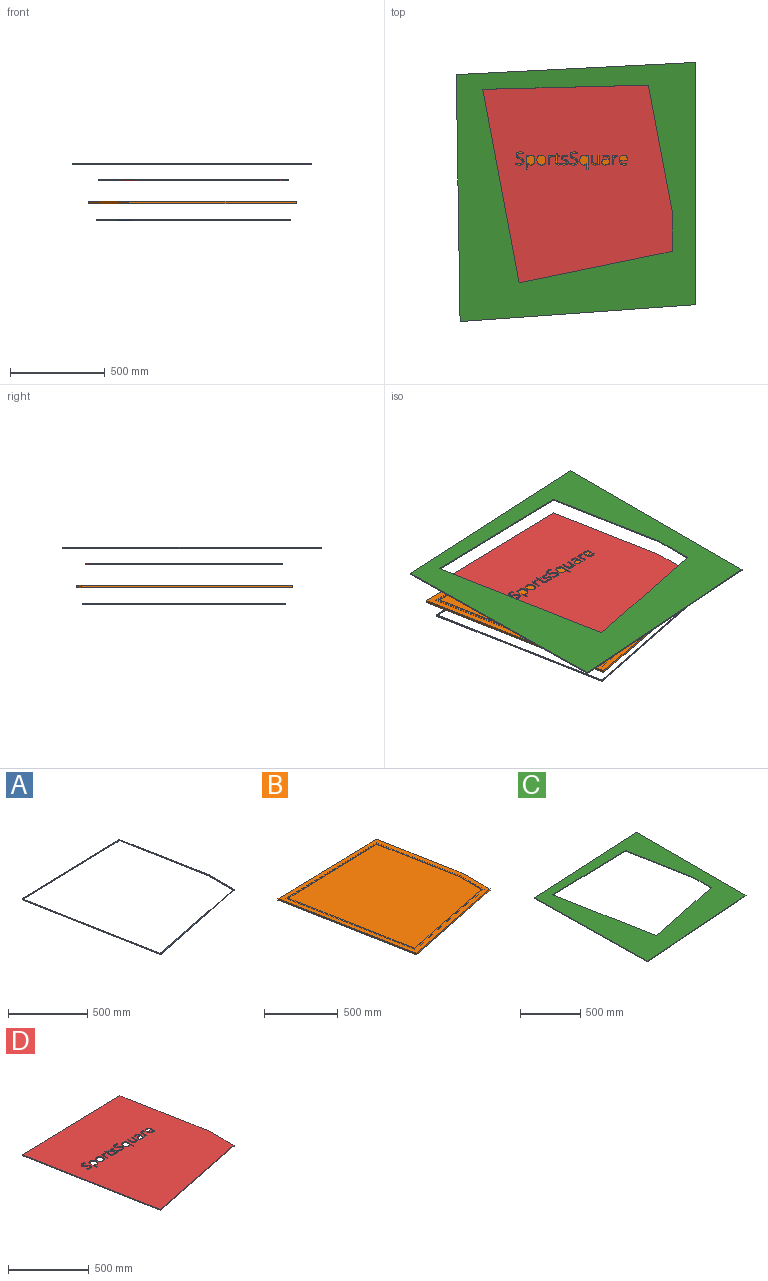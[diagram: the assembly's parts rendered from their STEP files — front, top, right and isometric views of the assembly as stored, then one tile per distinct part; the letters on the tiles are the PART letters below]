
ASSEMBLY  parts=4 mates=3
PART A: 22 faces, bbox 1023.6x1068.1x5 mm
  f0: cylinder r=5mm len=5.04mm, axis (0,0,-1), area 35.3mm2, adj f1,f19,f20,f21
  f1: plane 667.31x125.75mm, normal (-0.98,-0.19,0), area 3395.3mm2, adj f0,f2,f20,f21
  f2: cylinder r=5mm len=5mm, axis (0,0,-1), area 4.7mm2, adj f1,f3,f20,f21
  f3: plane 215x5mm, normal (-1,0,0), area 1075mm2, adj f2,f4,f20,f21
  f4: cylinder r=5mm len=5mm, axis (0,0,-1), area 34.2mm2, adj f3,f5,f20,f21
  f5: plane 812.02x166.92mm, normal (-0.2,0.98,0), area 4145mm2, adj f4,f6,f20,f21
  f6: cylinder r=5mm len=5.92mm, axis (0,0,-1), area 39.7mm2, adj f5,f7,f20,f21
  f7: plane 1026.83x192.78mm, normal (0.98,0.18,0), area 5223.8mm2, adj f6,f8,f20,f21
  f8: cylinder r=5mm len=5.92mm, axis (0,0,-1), area 43.3mm2, adj f7,f19,f20,f21
  f9: plane 671.02x126.45mm, normal (0.98,0.19,0), area 3414.1mm2, adj f10,f18,f20,f21
  f10: cylinder r=5mm len=5.04mm, axis (0,0,-1), area 35.3mm2, adj f9,f11,f20,f21
  f11: plane 887.15x22.61mm, normal (-0.03,1,0), area 4437.2mm2, adj f10,f12,f20,f21
  f12: cylinder r=5mm len=5.92mm, axis (0,0,-1), area 43.3mm2, adj f11,f13,f20,f21
  f13: plane 1035.44x194.39mm, normal (-0.98,-0.18,0), area 5267.7mm2, adj f12,f14,f20,f21
  f14: cylinder r=5mm len=5.92mm, axis (0,0,-1), area 39.7mm2, adj f13,f15,f20,f21
  f15: plane 819.2x168.4mm, normal (0.2,-0.98,0), area 4181.7mm2, adj f14,f16,f20,f21
  f16: cylinder r=5mm len=5mm, axis (0,0,-1), area 34.2mm2, adj f15,f17,f20,f21
  f17: plane 218.64x5mm, normal (1,0,0), area 1093.2mm2, adj f16,f18,f20,f21
  f18: cylinder r=5mm len=5mm, axis (0,0,-1), area 4.7mm2, adj f9,f17,f20,f21
  f19: plane 879.05x22.4mm, normal (0.03,-1,0), area 4396.7mm2, adj f0,f8,f20,f21
  f20: plane 1068.05x1023.6mm, normal (0,0,1), area 14809.9mm2, adj f0,f1,f2,f3,f4,f5,f6,f7
  f21: plane 1068.05x1023.6mm, normal (0,0,-1), area 14809.9mm2, adj f0,f1,f2,f3,f4,f5,f6,f7
PART B: 25 faces, bbox 1096.8x1141.5x12 mm
  f0: plane 964.09x24.57mm, normal (-0.03,1,0), area 11572.8mm2, adj f1,f9,f10,f11
  f1: plane 1116.92x209.69mm, normal (-0.98,-0.18,0), area 13637.2mm2, adj f0,f2,f10,f11
  f2: plane 887.09x182.36mm, normal (0.2,-0.98,0), area 10867.6mm2, adj f1,f3,f10,f11
  f3: plane 254.98x12mm, normal (1,0,0), area 3059.8mm2, adj f2,f9,f10,f11
  f4: plane 1022.14x191.9mm, normal (0.98,0.18,0), area 2080mm2, adj f5,f8,f10,f12
  f5: plane 875x22.3mm, normal (0.03,-1,0), area 1750.6mm2, adj f4,f6,f10,f12
  f6: plane 663.33x125mm, normal (-0.98,-0.19,0), area 1350mm2, adj f5,f7,f10,f12
  f7: plane 215x2mm, normal (-1,0,0), area 430mm2, adj f6,f8,f10,f12
  f8: plane 808.1x166.12mm, normal (-0.2,0.98,0), area 1650mm2, adj f4,f7,f10,f12
  f9: plane 704.16x132.69mm, normal (0.98,0.19,0), area 8598.6mm2, adj f0,f3,f10,f11
  f10: plane 1141.5x1096.78mm, normal (0,0,1), area 167382.4mm2, adj f0,f1,f2,f3,f4,f5,f6,f7
  f11: plane 1141.5x1096.78mm, normal (0,0,-1), area 119520.9mm2, adj f0,f1,f2,f3,f9,f17,f18,f19
  f12: plane 1044.44x1000mm, normal (0,0,1), area 828035.3mm2, adj f4,f5,f6,f7,f8
  f13: plane 885.12x22.56mm, normal (-0.03,1,0), area 7968.7mm2, adj f14,f22,f23,f24
  f14: plane 667.96x125.87mm, normal (0.98,0.19,0), area 6117.5mm2, adj f13,f15,f23,f24
  f15: plane 219.54x9mm, normal (1,0,0), area 1975.9mm2, adj f14,f16,f23,f24
  f16: plane 817.08x167.96mm, normal (0.2,-0.98,0), area 7507.5mm2, adj f15,f22,f23,f24
  f17: plane 675.39x127.27mm, normal (-0.98,-0.19,0), area 6185.5mm2, adj f11,f18,f21,f23
  f18: plane 901.32x22.97mm, normal (0.03,-1,0), area 8114.5mm2, adj f11,f17,f19,f23
  f19: plane 1050.15x197.16mm, normal (0.98,0.18,0), area 9616.4mm2, adj f11,f18,f20,f23
  f20: plane 831.44x170.92mm, normal (-0.2,0.98,0), area 7639.4mm2, adj f11,f19,f21,f23
  f21: plane 226.81x9mm, normal (-1,0,0), area 2041.3mm2, adj f11,f17,f20,f23
  f22: plane 1032.91x193.92mm, normal (-0.98,-0.18,0), area 9458.6mm2, adj f13,f16,f23,f24
  f23: plane 1073.12x1028.59mm, normal (0,0,-1), area 29611.3mm2, adj f13,f14,f15,f16,f17,f18,f19,f20
  f24: plane 1055.47x1011mm, normal (0,0,-1), area 846285.5mm2, adj f13,f14,f15,f16,f22
PART C: 11 faces, bbox 1265x1369.2x6 mm
  f0: plane 1022.14x191.9mm, normal (0.98,0.18,0), area 6240mm2, adj f1,f8,f9,f10
  f1: plane 875x22.3mm, normal (0.03,-1,0), area 5251.7mm2, adj f0,f2,f9,f10
  f2: plane 663.33x125mm, normal (-0.98,-0.19,0), area 4050mm2, adj f1,f3,f9,f10
  f3: plane 215x6mm, normal (-1,0,0), area 1290mm2, adj f2,f8,f9,f10
  f4: plane 1265x64.18mm, normal (-0.05,1,0), area 7599.8mm2, adj f5,f7,f9,f10
  f5: plane 1305x20mm, normal (-1,-0.02,0), area 7830.9mm2, adj f4,f6,f9,f10
  f6: plane 1245x89.18mm, normal (0.07,-1,0), area 7489.1mm2, adj f5,f7,f9,f10
  f7: plane 1280x6mm, normal (1,0,0), area 7680mm2, adj f4,f6,f9,f10
  f8: plane 808.1x166.12mm, normal (-0.2,0.98,0), area 4950mm2, adj f0,f3,f9,f10
  f9: plane 1369.18x1265mm, normal (0,0,1), area 794819mm2, adj f0,f1,f2,f3,f4,f5,f6,f7
  f10: plane 1369.18x1265mm, normal (0,0,-1), area 794819mm2, adj f0,f1,f2,f3,f4,f5,f6,f7
PART D: 216 faces, bbox 1000x1044.4x6 mm
  f0: extruded ~11.31x6mm, area 73.7mm2, adj f1,f213,f214,f215
  f1: extruded ~13.96x6.49mm, area 96mm2, adj f0,f2,f214,f215
  f2: extruded ~17.62x6mm, area 112mm2, adj f1,f3,f214,f215
  f3: extruded ~18.55x6mm, area 113.7mm2, adj f2,f4,f214,f215
  f4: plane 7.6x6mm, normal (1,0,0), area 45.6mm2, adj f3,f5,f214,f215
  f5: extruded ~9.1x6mm, area 57.2mm2, adj f4,f6,f214,f215
  f6: extruded ~9.74x6mm, area 58.8mm2, adj f5,f7,f214,f215
  f7: extruded ~11.87x6mm, area 74.7mm2, adj f6,f8,f214,f215
  f8: extruded ~8.33x6mm, area 57.7mm2, adj f7,f9,f214,f215
  f9: extruded ~6x5.77mm, area 36.1mm2, adj f8,f10,f214,f215
  f10: extruded ~6x4.73mm, area 38.2mm2, adj f9,f11,f214,f215
  f11: extruded ~10.08x6mm, area 65.9mm2, adj f10,f12,f214,f215
  f12: extruded ~13.51x8.02mm, area 95.2mm2, adj f11,f13,f214,f215
  f13: extruded ~12.1x6mm, area 78.3mm2, adj f12,f14,f214,f215
  f14: extruded ~12.47x6mm, area 85.9mm2, adj f13,f15,f214,f215
  f15: extruded ~15.59x6mm, area 99.5mm2, adj f14,f16,f214,f215
  f16: extruded ~18.59x6mm, area 114.6mm2, adj f15,f17,f214,f215
  f17: plane 6.86x6mm, normal (-0.94,0.34,0), area 43.7mm2, adj f16,f18,f214,f215
  f18: extruded ~16.32x6mm, area 100.9mm2, adj f17,f19,f214,f215
  f19: extruded ~9.79x6mm, area 62mm2, adj f18,f20,f214,f215
  f20: extruded ~7.46x6mm, area 51.5mm2, adj f19,f21,f214,f215
  f21: extruded ~6x5.77mm, area 35.9mm2, adj f20,f22,f214,f215
  f22: extruded ~6x4.39mm, area 36.5mm2, adj f21,f23,f214,f215
  f23: extruded ~9.44x6mm, area 61.9mm2, adj f22,f213,f214,f215
  f24: extruded ~15.52x6.94mm, area 105.7mm2, adj f25,f201,f214,f215
  f25: extruded ~9.07x6mm, area 56mm2, adj f24,f26,f214,f215
  f26: extruded ~6.88x6mm, area 54mm2, adj f25,f27,f214,f215
  f27: plane 6x0.56mm, normal (0,1,0), area 3.4mm2, adj f26,f28,f214,f215
  f28: extruded ~8.44x6mm, area 50.8mm2, adj f27,f29,f214,f215
  f29: plane 20.92x6mm, normal (-1,0,0), area 125.5mm2, adj f28,f30,f214,f215
  f30: plane 7.7x6mm, normal (0,1,0), area 46.2mm2, adj f29,f31,f214,f215
  f31: plane 73.65x6mm, normal (1,0,0), area 441.9mm2, adj f30,f32,f214,f215
  f32: plane 6.26x6mm, normal (0,-1,0), area 37.6mm2, adj f31,f33,f214,f215
  f33: plane 6.96x6mm, normal (-0.99,-0.15,0), area 42.2mm2, adj f32,f34,f214,f215
  f34: plane 6x0.37mm, normal (0,-1,0), area 2.2mm2, adj f33,f35,f214,f215
  f35: extruded ~6.91x6.04mm, area 55.7mm2, adj f34,f36,f214,f215
  f36: extruded ~9.05x6mm, area 55.9mm2, adj f35,f37,f214,f215
  f37: extruded ~15.6x6.92mm, area 106.2mm2, adj f36,f38,f214,f215
  f38: extruded ~19.38x6mm, area 123.2mm2, adj f37,f201,f214,f215
  f39: extruded ~8.77x6mm, area 55.9mm2, adj f40,f202,f214,f215
  f40: extruded ~6.07x6mm, area 36.6mm2, adj f39,f41,f214,f215
  f41: plane 7.14x6mm, normal (-0.99,0.15,0), area 43.3mm2, adj f40,f42,f214,f215
  f42: extruded ~6x5.57mm, area 33.7mm2, adj f41,f43,f214,f215
  f43: extruded ~10.55x6mm, area 72.4mm2, adj f42,f44,f214,f215
  f44: extruded ~12.47x6mm, area 81.1mm2, adj f43,f45,f214,f215
  f45: plane 27.28x6mm, normal (-1,0,0), area 163.7mm2, adj f44,f46,f214,f215
  f46: plane 7.7x6mm, normal (0,1,0), area 46.2mm2, adj f45,f47,f214,f215
  f47: plane 50.83x6mm, normal (1,0,0), area 305mm2, adj f46,f48,f214,f215
  f48: plane 6.35x6mm, normal (0,-1,0), area 38.1mm2, adj f47,f49,f214,f215
  f49: plane 9.41x6mm, normal (-1,-0.09,0), area 56.7mm2, adj f48,f50,f214,f215
  f50: plane 6x0.37mm, normal (0,-1,0), area 2.2mm2, adj f49,f202,f214,f215
  f51: extruded ~6x5.98mm, area 40mm2, adj f52,f203,f214,f215
  f52: extruded ~6x3.95mm, area 23.8mm2, adj f51,f53,f214,f215
  f53: extruded ~6x3.01mm, area 18.5mm2, adj f52,f54,f214,f215
  f54: plane 6x5.89mm, normal (-1,0,0), area 35.3mm2, adj f53,f55,f214,f215
  f55: extruded ~6x3.68mm, area 22.9mm2, adj f54,f56,f214,f215
  f56: extruded ~6x4.39mm, area 26.5mm2, adj f55,f57,f214,f215
  f57: extruded ~15.54x14.74mm, area 147.4mm2, adj f56,f58,f214,f215
  f58: plane 30.24x6mm, normal (1,0,0), area 181.5mm2, adj f57,f59,f214,f215
  f59: plane 7.29x6mm, normal (0,1,0), area 43.7mm2, adj f58,f60,f214,f215
  f60: plane 6x3.71mm, normal (1,0,0), area 22.3mm2, adj f59,f61,f214,f215
  f61: plane 7.29x6mm, normal (0.4,-0.92,0), area 47.8mm2, adj f60,f62,f214,f215
  f62: plane 10.85x6mm, normal (0.96,-0.29,0), area 67.9mm2, adj f61,f63,f214,f215
  f63: plane 6x4.45mm, normal (0,-1,0), area 26.7mm2, adj f62,f64,f214,f215
  f64: plane 11.78x6mm, normal (-1,0,0), area 70.7mm2, adj f63,f65,f214,f215
  f65: plane 14.75x6mm, normal (0,-1,0), area 88.5mm2, adj f64,f66,f214,f215
  f66: plane 6x5.98mm, normal (-1,0,0), area 35.9mm2, adj f65,f67,f214,f215
  f67: plane 14.75x6mm, normal (0,1,0), area 88.5mm2, adj f66,f68,f214,f215
  f68: plane 29.92x6mm, normal (-1,0,0), area 179.5mm2, adj f67,f203,f214,f215
  f69: extruded ~8.4x6mm, area 55.3mm2, adj f70,f204,f214,f215
  f70: extruded ~10.94x6mm, area 75.9mm2, adj f69,f71,f214,f215
  f71: extruded ~14.84x6mm, area 93.5mm2, adj f70,f72,f214,f215
  f72: extruded ~15.76x6mm, area 97.5mm2, adj f71,f73,f214,f215
  f73: plane 7.14x6mm, normal (1,0,0), area 42.8mm2, adj f72,f74,f214,f215
  f74: extruded ~7.86x6mm, area 50.4mm2, adj f73,f75,f214,f215
  f75: extruded ~8.1x6mm, area 49.1mm2, adj f74,f76,f214,f215
  f76: extruded ~9.27x6mm, area 57.4mm2, adj f75,f77,f214,f215
  f77: extruded ~6x5.87mm, area 42.3mm2, adj f76,f78,f214,f215
  f78: extruded ~6x5.08mm, area 35.4mm2, adj f77,f79,f214,f215
  f79: extruded ~10.05x6mm, area 67.5mm2, adj f78,f80,f214,f215
  f80: extruded ~10.08x6mm, area 66.7mm2, adj f79,f81,f214,f215
  f81: extruded ~6x4.47mm, area 38.2mm2, adj f80,f82,f214,f215
  f82: extruded ~6x5.97mm, area 37.3mm2, adj f81,f83,f214,f215
  f83: extruded ~9.82x6mm, area 69.1mm2, adj f82,f84,f214,f215
  f84: extruded ~13.86x6mm, area 87.3mm2, adj f83,f85,f214,f215
  f85: extruded ~16.06x6mm, area 99.1mm2, adj f84,f86,f214,f215
  f86: plane 6.26x6mm, normal (-0.92,0.4,0), area 41mm2, adj f85,f87,f214,f215
  f87: extruded ~13.86x6mm, area 85.8mm2, adj f86,f88,f214,f215
  f88: extruded ~8.26x6mm, area 51.2mm2, adj f87,f89,f214,f215
  f89: extruded ~6x4.73mm, area 34.5mm2, adj f88,f90,f214,f215
  f90: extruded ~6x3.48mm, area 22.2mm2, adj f89,f91,f214,f215
  f91: extruded ~6x3.36mm, area 26.2mm2, adj f90,f92,f214,f215
  f92: extruded ~8.9x6mm, area 58mm2, adj f91,f204,f214,f215
  f93: extruded ~11.31x6mm, area 73.7mm2, adj f94,f205,f214,f215
  f94: extruded ~13.96x6.49mm, area 96mm2, adj f93,f95,f214,f215
  f95: extruded ~17.62x6mm, area 112mm2, adj f94,f96,f214,f215
  f96: extruded ~18.55x6mm, area 113.7mm2, adj f95,f97,f214,f215
  f97: plane 7.6x6mm, normal (1,0,0), area 45.6mm2, adj f96,f98,f214,f215
  f98: extruded ~9.1x6mm, area 57.2mm2, adj f97,f99,f214,f215
  f99: extruded ~9.74x6mm, area 58.8mm2, adj f98,f100,f214,f215
  f100: extruded ~11.87x6mm, area 74.7mm2, adj f99,f101,f214,f215
  f101: extruded ~8.33x6mm, area 57.7mm2, adj f100,f102,f214,f215
  f102: extruded ~6x5.77mm, area 36.1mm2, adj f101,f103,f214,f215
  f103: extruded ~6x4.73mm, area 38.2mm2, adj f102,f104,f214,f215
  f104: extruded ~10.08x6mm, area 65.9mm2, adj f103,f105,f214,f215
  f105: extruded ~13.51x8.02mm, area 95.2mm2, adj f104,f106,f214,f215
  f106: extruded ~12.1x6mm, area 78.3mm2, adj f105,f107,f214,f215
  f107: extruded ~12.47x6mm, area 85.9mm2, adj f106,f108,f214,f215
  f108: extruded ~15.59x6mm, area 99.5mm2, adj f107,f109,f214,f215
  f109: extruded ~18.59x6mm, area 114.6mm2, adj f108,f110,f214,f215
  f110: plane 6.86x6mm, normal (-0.94,0.34,0), area 43.7mm2, adj f109,f111,f214,f215
  f111: extruded ~16.32x6mm, area 100.9mm2, adj f110,f112,f214,f215
  f112: extruded ~9.79x6mm, area 62mm2, adj f111,f113,f214,f215
  f113: extruded ~7.46x6mm, area 51.5mm2, adj f112,f114,f214,f215
  f114: extruded ~6x5.77mm, area 35.9mm2, adj f113,f115,f214,f215
  f115: extruded ~6x4.39mm, area 36.5mm2, adj f114,f116,f214,f215
  f116: extruded ~9.44x6mm, area 61.9mm2, adj f115,f205,f214,f215
  f117: extruded ~16.04x7.75mm, area 111.6mm2, adj f118,f206,f214,f215
  f118: extruded ~15.36x6.92mm, area 104.8mm2, adj f117,f119,f214,f215
  f119: extruded ~19.29x6mm, area 122.7mm2, adj f118,f120,f214,f215
  f120: extruded ~19.48x6mm, area 123.9mm2, adj f119,f121,f214,f215
  f121: extruded ~15.49x7mm, area 105.8mm2, adj f120,f122,f214,f215
  f122: extruded ~16.04x7.89mm, area 111.9mm2, adj f121,f123,f214,f215
  f123: plane 6x0.43mm, normal (0,-1,0), area 2.6mm2, adj f122,f124,f214,f215
  f124: plane 6.96x6mm, normal (0.99,-0.16,0), area 42.3mm2, adj f123,f125,f214,f215
  f125: plane 6.07x6mm, normal (0,-1,0), area 36.4mm2, adj f124,f126,f214,f215
  f126: plane 73.65x6mm, normal (-1,0,0), area 441.9mm2, adj f125,f127,f214,f215
  f127: plane 7.7x6mm, normal (0,1,0), area 46.2mm2, adj f126,f128,f214,f215
  f128: plane 21.76x6mm, normal (1,0,0), area 130.5mm2, adj f127,f129,f214,f215
  f129: extruded ~7.88x6mm, area 47.4mm2, adj f128,f206,f214,f215
  f130: plane 7.79x6mm, normal (0,-1,0), area 46.7mm2, adj f131,f207,f214,f215
  f131: plane 32.97x6mm, normal (-1,0,0), area 197.8mm2, adj f130,f132,f214,f215
  f132: extruded ~9.28x6mm, area 59.5mm2, adj f131,f133,f214,f215
  f133: extruded ~8.85x6mm, area 57.8mm2, adj f132,f134,f214,f215
  f134: extruded ~11.66x6mm, area 77.2mm2, adj f133,f135,f214,f215
  f135: extruded ~14.24x6mm, area 90mm2, adj f134,f136,f214,f215
  f136: plane 26.71x6mm, normal (1,0,0), area 160.3mm2, adj f135,f137,f214,f215
  f137: plane 7.7x6mm, normal (0,-1,0), area 46.2mm2, adj f136,f138,f214,f215
  f138: plane 50.83x6mm, normal (-1,0,0), area 305mm2, adj f137,f139,f214,f215
  f139: plane 6.35x6mm, normal (0,1,0), area 38.1mm2, adj f138,f140,f214,f215
  f140: plane 6.81x6mm, normal (0.99,0.16,0), area 41.4mm2, adj f139,f141,f214,f215
  f141: plane 6x0.42mm, normal (0,1,0), area 2.5mm2, adj f140,f142,f214,f215
  f142: extruded ~6.56x6mm, area 53.1mm2, adj f141,f143,f214,f215
  f143: extruded ~9.59x6mm, area 59.2mm2, adj f142,f144,f214,f215
  f144: extruded ~13.88x6mm, area 89.6mm2, adj f143,f145,f214,f215
  f145: extruded ~14.1x6mm, area 91.5mm2, adj f144,f207,f214,f215
  f146: plane 6x5.71mm, normal (0,1,0), area 34.3mm2, adj f147,f208,f214,f215
  f147: plane 7.24x6mm, normal (0.98,0.21,0), area 44.4mm2, adj f146,f148,f214,f215
  f148: plane 6x0.37mm, normal (0,1,0), area 2.2mm2, adj f147,f149,f214,f215
  f149: extruded ~7.58x6.48mm, area 60.4mm2, adj f148,f150,f214,f215
  f150: extruded ~9.45x6mm, area 58mm2, adj f149,f151,f214,f215
  f151: extruded ~11.84x6mm, area 76.6mm2, adj f150,f152,f214,f215
  f152: extruded ~11.09x6mm, area 73.5mm2, adj f151,f153,f214,f215
  f153: extruded ~24.62x16.13mm, area 198.4mm2, adj f152,f154,f214,f215
  f154: plane 8.62x6mm, normal (0.03,-1,0), area 51.8mm2, adj f153,f155,f214,f215
  f155: plane 6x3.16mm, normal (1,0,0), area 19mm2, adj f154,f156,f214,f215
  f156: extruded ~8.83x6mm, area 56.4mm2, adj f155,f157,f214,f215
  f157: extruded ~8.24x6mm, area 53.9mm2, adj f156,f158,f214,f215
  f158: extruded ~14.37x6mm, area 90mm2, adj f157,f159,f214,f215
  f159: plane 6x5.89mm, normal (0.93,0.37,0), area 38.1mm2, adj f158,f160,f214,f215
  f160: extruded ~8.23x6mm, area 53.1mm2, adj f159,f161,f214,f215
  f161: extruded ~8.99x6mm, area 54.5mm2, adj f160,f162,f214,f215
  f162: extruded ~13.47x6mm, area 86.3mm2, adj f161,f163,f214,f215
  f163: extruded ~12.93x6mm, area 84.3mm2, adj f162,f208,f214,f215
  f164: extruded ~8.79x6mm, area 53mm2, adj f165,f209,f214,f215
  f165: extruded ~17.79x6.87mm, area 117.8mm2, adj f164,f166,f214,f215
  f166: extruded ~19.05x6.52mm, area 123.9mm2, adj f165,f167,f214,f215
  f167: extruded ~19.54x6.05mm, area 125.3mm2, adj f166,f168,f214,f215
  f168: extruded ~16.26x7.23mm, area 110.6mm2, adj f167,f169,f214,f215
  f169: extruded ~15.11x6.28mm, area 101.4mm2, adj f168,f170,f214,f215
  f170: extruded ~16.58x6mm, area 107.4mm2, adj f169,f171,f214,f215
  f171: plane 6x4.87mm, normal (-1,0,0), area 29.2mm2, adj f170,f172,f214,f215
  f172: plane 35.01x6mm, normal (0,1,0), area 210mm2, adj f171,f173,f214,f215
  f173: extruded ~13.59x6mm, area 87.8mm2, adj f172,f174,f214,f215
  f174: extruded ~12.08x6mm, area 80mm2, adj f173,f175,f214,f215
  f175: extruded ~16.22x6mm, area 100.2mm2, adj f174,f176,f214,f215
  f176: plane 6.87x6mm, normal (-1,0,0), area 41.2mm2, adj f175,f209,f214,f215
  f177: extruded ~8.77x6mm, area 55.9mm2, adj f178,f210,f214,f215
  f178: extruded ~6.07x6mm, area 36.6mm2, adj f177,f179,f214,f215
  f179: plane 7.14x6mm, normal (-0.99,0.15,0), area 43.3mm2, adj f178,f180,f214,f215
  f180: extruded ~6x5.57mm, area 33.7mm2, adj f179,f181,f214,f215
  f181: extruded ~10.55x6mm, area 72.4mm2, adj f180,f182,f214,f215
  f182: extruded ~12.47x6mm, area 81.1mm2, adj f181,f183,f214,f215
  f183: plane 27.28x6mm, normal (-1,0,0), area 163.7mm2, adj f182,f184,f214,f215
  f184: plane 7.7x6mm, normal (0,1,0), area 46.2mm2, adj f183,f185,f214,f215
  f185: plane 50.83x6mm, normal (1,0,0), area 305mm2, adj f184,f186,f214,f215
  f186: plane 6.35x6mm, normal (0,-1,0), area 38.1mm2, adj f185,f187,f214,f215
  f187: plane 9.41x6mm, normal (-1,-0.09,0), area 56.7mm2, adj f186,f188,f214,f215
  f188: plane 6x0.37mm, normal (0,-1,0), area 2.2mm2, adj f187,f210,f214,f215
  f189: extruded ~19.2x6.28mm, area 124mm2, adj f190,f211,f214,f215
  f190: extruded ~19.42x6.26mm, area 125.2mm2, adj f189,f191,f214,f215
  f191: extruded ~17.3x6.98mm, area 115.5mm2, adj f190,f192,f214,f215
  f192: extruded ~12.11x6mm, area 76.1mm2, adj f191,f193,f214,f215
  f193: extruded ~9.19x8.16mm, area 74.8mm2, adj f192,f194,f214,f215
  f194: extruded ~14.01x6mm, area 86.5mm2, adj f193,f195,f214,f215
  f195: extruded ~19.36x6.22mm, area 124.8mm2, adj f194,f196,f214,f215
  f196: extruded ~17.26x6.94mm, area 115.2mm2, adj f195,f211,f214,f215
  f197: plane 875x22.3mm, normal (-0.03,1,0), area 5251.7mm2, adj f198,f212,f214,f215
  f198: plane 1022.14x191.9mm, normal (-0.98,-0.18,0), area 6240mm2, adj f197,f199,f214,f215
  f199: plane 808.1x166.12mm, normal (0.2,-0.98,0), area 4950mm2, adj f198,f200,f214,f215
  f200: plane 215x6mm, normal (1,0,0), area 1290mm2, adj f199,f212,f214,f215
  f201: extruded ~19.46x6mm, area 123.9mm2, adj f24,f38,f214,f215
  f202: extruded ~7.65x6.81mm, area 62mm2, adj f39,f50,f214,f215
  f203: extruded ~7.04x6mm, area 45.2mm2, adj f51,f68,f214,f215
  f204: extruded ~12.21x6.63mm, area 84mm2, adj f69,f92,f214,f215
  f205: extruded ~14.68x8.16mm, area 101.6mm2, adj f93,f116,f214,f215
  f206: plane 6x0.61mm, normal (0,1,0), area 3.7mm2, adj f117,f129,f214,f215
  f207: plane 33.26x6mm, normal (1,0,0), area 199.5mm2, adj f130,f145,f214,f215
  f208: plane 34.7x6mm, normal (-1,0,0), area 208.2mm2, adj f146,f163,f214,f215
  f209: extruded ~7.72x6mm, area 48.8mm2, adj f164,f176,f214,f215
  f210: extruded ~7.65x6.81mm, area 62mm2, adj f177,f188,f214,f215
  f211: extruded ~16.94x7.1mm, area 113.8mm2, adj f189,f196,f214,f215
  f212: plane 663.33x125mm, normal (0.98,0.19,0), area 4050mm2, adj f197,f200,f214,f215
  f213: extruded ~14.68x8.16mm, area 101.6mm2, adj f0,f23,f214,f215
  f214: plane 1044.44x1000mm, normal (0,0,1), area 813183.4mm2, adj f0,f1,f2,f3,f4,f5,f6,f7
  f215: plane 1044.44x1000mm, normal (0,0,-1), area 813183.4mm2, adj f0,f1,f2,f3,f4,f5,f6,f7
PLACE A t=(-2348.63,-665.08,1470.26)mm
PLACE B t=(-2328.97,-636.14,1561.26)mm
PLACE C t=(-2446.58,-747.45,1769.39)mm
PLACE D t=(-2833.73,-1269.05,1681.26)mm
MATE slider A.f21 <-> B.f23  axis (0,0,-1) through (-2802.72,-1222.86,1470.26)mm
MATE slider C.f9 <-> D.f214  axis (0,0,1) through (-2990.64,-194.79,1775.39)mm
MATE slider D.f215 <-> B.f12  axis (0,0,-1) through (-2990.64,-194.79,1681.26)mm
